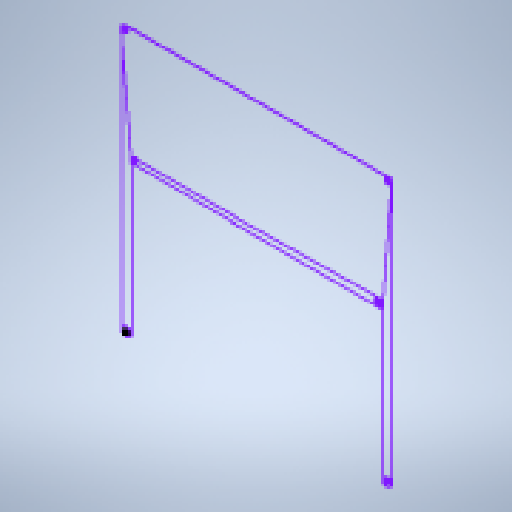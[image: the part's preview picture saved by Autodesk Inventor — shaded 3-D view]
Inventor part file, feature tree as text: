
AUTODESK INVENTOR PART (.ipt)
format: ipt  version: 2023 (Build 270158000, 158)  size: 132,608 bytes
history: native  units: mm
features: sketch x1
ambient origin geometry x8: Origin, YZ Plane, XZ Plane, XY Plane, X Axis, Y Axis, Z Axis, Center Point
feature tree (1):
  sketch  "Sketch1"
